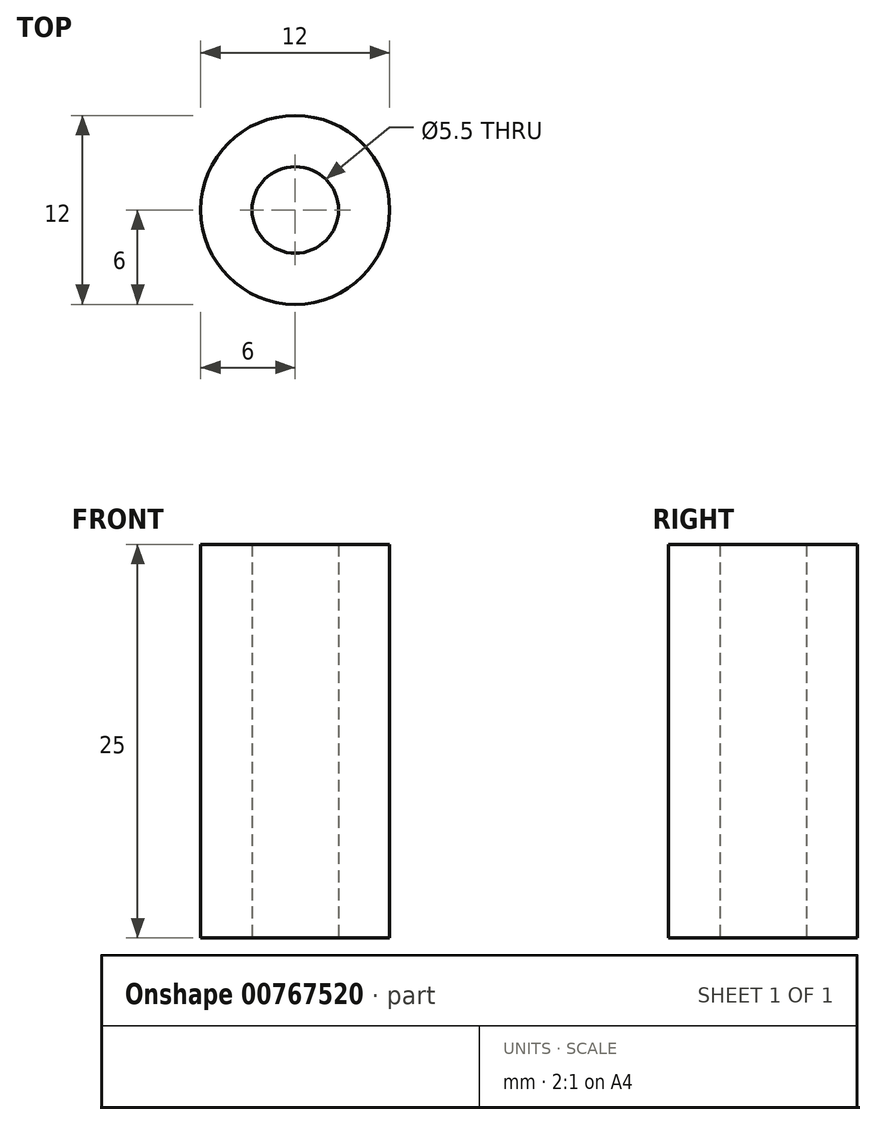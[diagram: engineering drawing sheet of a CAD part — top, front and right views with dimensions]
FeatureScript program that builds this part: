
annotation { "Feature Type Name" : "Feature", "Feature Type Description" : "" }
export const myFeature = defineFeature(function(context is Context, id is Id, definition is map)
    precondition{}
    {
        {
            var Q0;
            Q0=qCreatedBy(makeId("Top.planeOp"),FACE);
            var sketch = newSketch(context, id + "F0", { "sketchPlane" : qUnion([Q0])});
            skCircle(sketch, "E0", {"center": v(0, 0) * mm, "radius": 6 * mm});
            skCircle(sketch, "E1", {"center": v(0, 0) * mm, "radius": 2.75 * mm});
            skSolve(sketch);
        }
        {
            var Q0;
            Q0=makeQuery(id+"F0.imprint","IMPRINT",FACE,{"disambiguationData":[TD([[makeQuery(id+"F0.imprint","IMPRINT",EDGE,{"derivedFrom":sQuery(id+"F0.wireOp",EDGE,"E0")}),1.0]])]});
            extrude(context, id + "F1", {"entities" : qUnion([Q0]), "depth" : 25 * mm, "offsetDistance" : 25 * mm});
        }
    });
